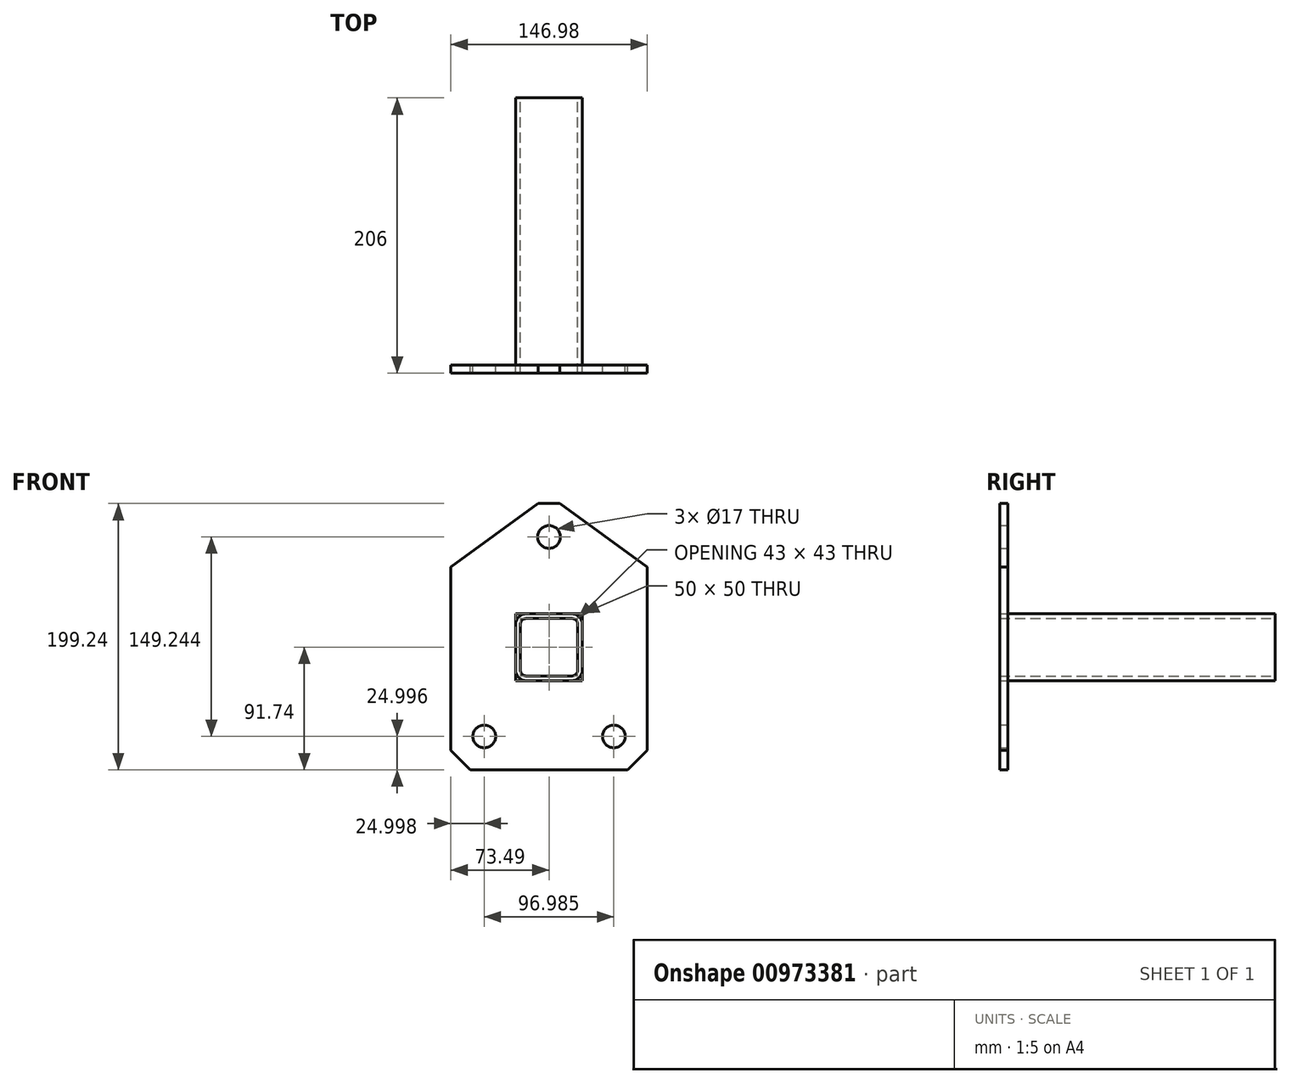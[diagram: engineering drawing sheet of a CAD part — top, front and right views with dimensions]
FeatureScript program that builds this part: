
annotation { "Feature Type Name" : "Feature", "Feature Type Description" : "" }
export const myFeature = defineFeature(function(context is Context, id is Id, definition is map)
    precondition{}
    {
        {
            var Q0;
            Q0=qCreatedBy(makeId("Front.planeOp"),FACE);
            var sketch = newSketch(context, id + "F0", { "sketchPlane" : qUnion([Q0])});
            skCircle(sketch, "E0.cCircle", {"center": v(0, 0) * mm, "radius": 82.5 * mm, "construction": true});
            skLineSegment(sketch, "E0.0", {"start": v(0, 82.5) * mm, "end": v(78.46, 25.5) * mm, "construction": true});
            skLineSegment(sketch, "E0.1", {"start": v(78.46, 25.5) * mm, "end": v(48.5, -66.74) * mm, "construction": true});
            skLineSegment(sketch, "E0.2", {"start": v(48.5, -66.74) * mm, "end": v(-48.5, -66.74) * mm, "construction": true});
            skLineSegment(sketch, "E0.3", {"start": v(-48.5, -66.74) * mm, "end": v(-78.46, 25.5) * mm, "construction": true});
            skLineSegment(sketch, "E0.4", {"start": v(-78.46, 25.5) * mm, "end": v(0, 82.5) * mm, "construction": true});
            skCircle(sketch, "E1", {"center": v(0, 82.5) * mm, "radius": 8.5 * mm});
            skCircle(sketch, "E2", {"center": v(-48.5, -66.74) * mm, "radius": 8.5 * mm});
            skCircle(sketch, "E3", {"center": v(48.5, -66.74) * mm, "radius": 8.5 * mm});
            skLineSegment(sketch, "E4.bottom", {"start": v(-25, 25) * mm, "end": v(25, 25) * mm});
            skLineSegment(sketch, "E4.top", {"start": v(-25, -25) * mm, "end": v(25, -25) * mm});
            skLineSegment(sketch, "E4.left", {"start": v(-25, 25) * mm, "end": v(-25, -25) * mm});
            skLineSegment(sketch, "E4.right", {"start": v(25, 25) * mm, "end": v(25, -25) * mm});
            skLineSegment(sketch, "E5", {"start": v(0, 107.5) * mm, "end": v(-8.12, 107.5) * mm});
            skLineSegment(sketch, "E6", {"start": v(-8.12, 107.5) * mm, "end": v(-73.5, 60) * mm});
            skLineSegment(sketch, "E7", {"start": v(-73.5, 60) * mm, "end": v(-73.5, -77.1) * mm});
            skLineSegment(sketch, "E8", {"start": v(-73.5, -77.1) * mm, "end": v(-58.85, -91.74) * mm});
            skLineSegment(sketch, "E9", {"start": v(-58.85, -91.74) * mm, "end": v(0, -91.74) * mm});
            skLineSegment(sketch, "E10", {"start": v(0, 0) * mm, "end": v(0, 128.46) * mm, "construction": true});
            skLineSegment(sketch, "E11.MirrorCS", {"start": v(0, 107.5) * mm, "end": v(8.12, 107.5) * mm});
            skLineSegment(sketch, "E12.MirrorCS", {"start": v(8.12, 107.5) * mm, "end": v(73.5, 60) * mm});
            skLineSegment(sketch, "E13.MirrorCS", {"start": v(73.5, 60) * mm, "end": v(73.5, -77.1) * mm});
            skLineSegment(sketch, "E14.MirrorCS", {"start": v(73.5, -77.1) * mm, "end": v(58.85, -91.74) * mm});
            skLineSegment(sketch, "E15.MirrorCS", {"start": v(58.85, -91.74) * mm, "end": v(0, -91.74) * mm});
            skSolve(sketch);
        }
        {
            var Q0;
            Q0 = qSketchRegion(id + "F0", true);
            extrude(context, id + "F1", {"entities" : qUnion([Q0]), "depth" : 6 * mm, "offsetDistance" : 25 * mm});
        }
        {
            var Q0;
            Q0=qCreatedBy(makeId("Front.planeOp"),FACE);
            var sketch = newSketch(context, id + "F2", { "sketchPlane" : qUnion([Q0])});
            skPoint(sketch, "E16.middle", {"position": v(0, 0) * mm});
            skLineSegment(sketch, "E17.bottom", {"start": v(-17, 25) * mm, "end": v(17, 25) * mm});
            skLineSegment(sketch, "E17.top", {"start": v(-17, -25) * mm, "end": v(17, -25) * mm});
            skLineSegment(sketch, "E17.left", {"start": v(-25, 17) * mm, "end": v(-25, -17) * mm});
            skLineSegment(sketch, "E17.right", {"start": v(25, 17) * mm, "end": v(25, -17) * mm});
            skPoint(sketch, "E18.visualSharp", {"position": v(-25, 25) * mm});
            skArc(sketch, "E18.filletArc", {"start": v(-17, 25) * mm, "mid": v(-22.66, 22.66) * mm, "end": v(-25, 17) * mm});
            skPoint(sketch, "E19.visualSharp", {"position": v(-25, -25) * mm});
            skArc(sketch, "E19.filletArc", {"start": v(-25, -17) * mm, "mid": v(-22.66, -22.66) * mm, "end": v(-17, -25) * mm});
            skPoint(sketch, "E20.visualSharp", {"position": v(25, -25) * mm});
            skArc(sketch, "E20.filletArc", {"start": v(17, -25) * mm, "mid": v(22.66, -22.66) * mm, "end": v(25, -17) * mm});
            skPoint(sketch, "E21.visualSharp", {"position": v(25, 25) * mm});
            skArc(sketch, "E21.filletArc", {"start": v(25, 17) * mm, "mid": v(22.66, 22.66) * mm, "end": v(17, 25) * mm});
            skArc(sketch, "E22.0", {"start": v(-17, 21.5) * mm, "mid": v(-20.18, 20.18) * mm, "end": v(-21.5, 17) * mm});
            skLineSegment(sketch, "E22.1", {"start": v(-21.5, 17) * mm, "end": v(-21.5, -17) * mm});
            skLineSegment(sketch, "E22.2", {"start": v(-17, 21.5) * mm, "end": v(17, 21.5) * mm});
            skArc(sketch, "E22.3", {"start": v(-21.5, -17) * mm, "mid": v(-20.18, -20.18) * mm, "end": v(-17, -21.5) * mm});
            skArc(sketch, "E22.4", {"start": v(21.5, 17) * mm, "mid": v(20.18, 20.18) * mm, "end": v(17, 21.5) * mm});
            skLineSegment(sketch, "E22.5", {"start": v(21.5, 17) * mm, "end": v(21.5, -17) * mm});
            skArc(sketch, "E22.6", {"start": v(17, -21.5) * mm, "mid": v(20.18, -20.18) * mm, "end": v(21.5, -17) * mm});
            skLineSegment(sketch, "E22.7", {"start": v(-17, -21.5) * mm, "end": v(17, -21.5) * mm});
            skSolve(sketch);
        }
        {
            var Q0;
            Q0 = qSketchRegion(id + "F2", true);
            extrude(context, id + "F3", {"entities" : qUnion([Q0]), "depth" : 6 * mm, "offsetDistance" : 25 * mm, "hasSecondDirection" : true, "secondDirectionOppositeDirection" : true, "secondDirectionDepth" : 200 * mm});
        }
    });
